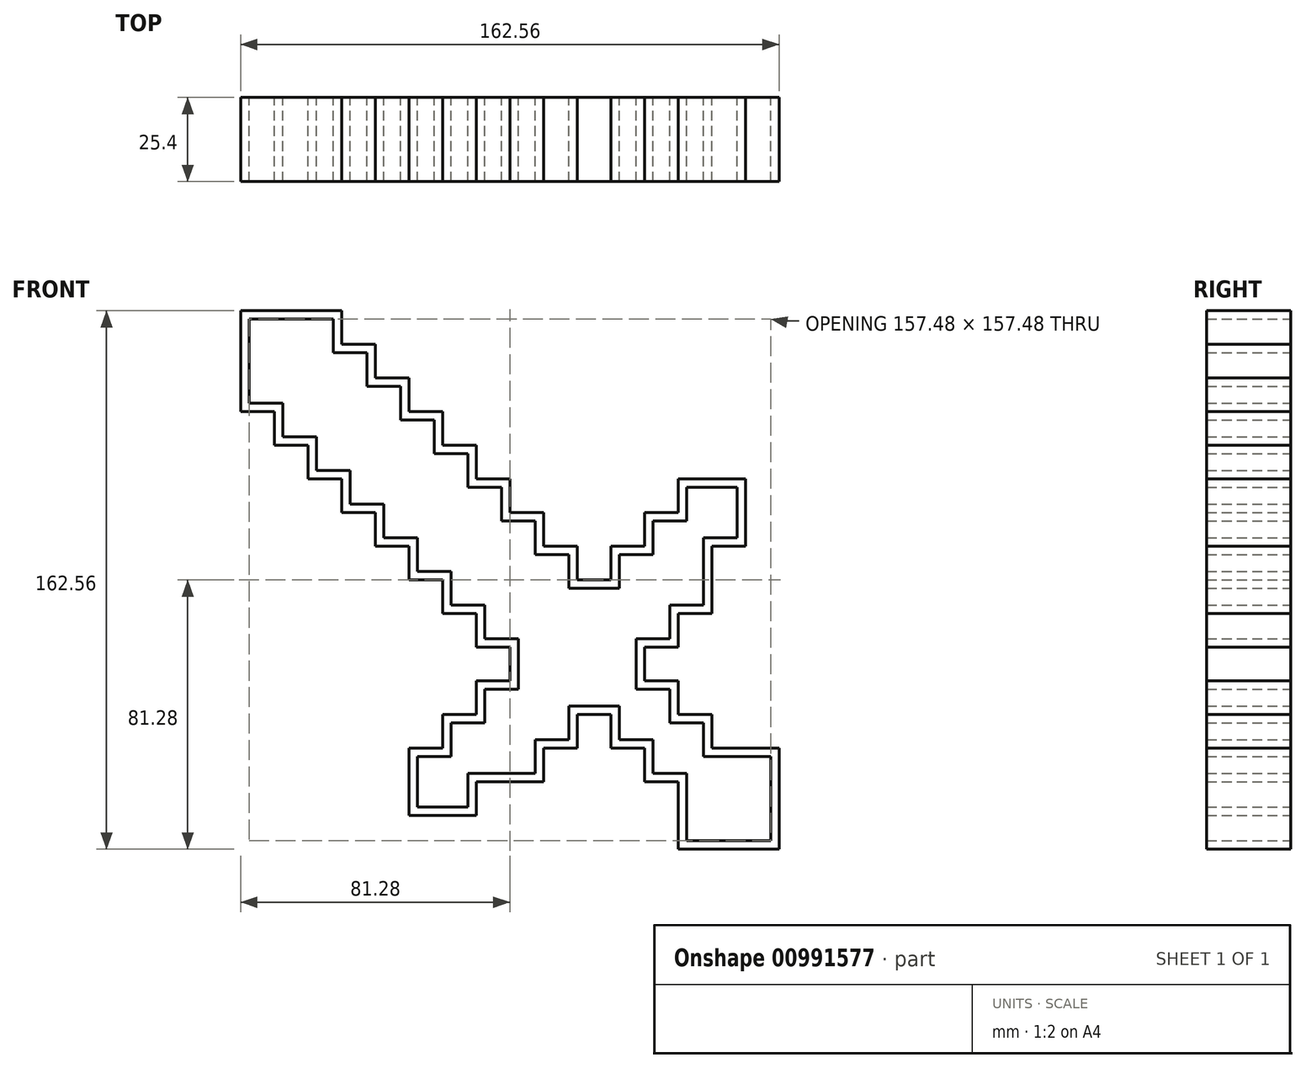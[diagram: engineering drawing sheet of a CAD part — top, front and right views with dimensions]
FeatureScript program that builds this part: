
annotation { "Feature Type Name" : "Feature", "Feature Type Description" : "" }
export const myFeature = defineFeature(function(context is Context, id is Id, definition is map)
    precondition{}
    {
        {
            var Q0;
            Q0=qCreatedBy(makeId("Front.planeOp"),FACE);
            var sketch = newSketch(context, id + "F0", { "sketchPlane" : qUnion([Q0])});
            skLineSegment(sketch, "E0.bottom", {"start": v(-6.87, -60.96) * mm, "end": v(23.61, -60.96) * mm});
            skLineSegment(sketch, "E0.top", {"start": v(3.3, -30.48) * mm, "end": v(23.61, -30.48) * mm});
            skLineSegment(sketch, "E0.left", {"start": v(-6.87, -60.96) * mm, "end": v(-6.87, -40.64) * mm});
            skLineSegment(sketch, "E0.right", {"start": v(23.61, -60.96) * mm, "end": v(23.61, -30.48) * mm});
            skLineSegment(sketch, "E1.bottom", {"start": v(-6.87, -40.64) * mm, "end": v(-17.03, -40.64) * mm});
            skLineSegment(sketch, "E1.top", {"start": v(3.3, -20.32) * mm, "end": v(-17.03, -20.32) * mm});
            skLineSegment(sketch, "E1.left", {"start": v(3.3, -30.48) * mm, "end": v(3.3, -20.32) * mm});
            skLineSegment(sketch, "E1.right", {"start": v(-17.03, -40.64) * mm, "end": v(-17.03, -30.48) * mm});
            skLineSegment(sketch, "E2.bottom", {"start": v(-17.03, -30.48) * mm, "end": v(-27.19, -30.48) * mm});
            skLineSegment(sketch, "E2.top", {"start": v(-6.87, -10.16) * mm, "end": v(-17.03, -10.16) * mm});
            skLineSegment(sketch, "E2.left", {"start": v(-6.87, -20.32) * mm, "end": v(-6.87, -10.16) * mm});
            skLineSegment(sketch, "E2.right", {"start": v(-27.19, -30.48) * mm, "end": v(-27.19, -20.32) * mm});
            skLineSegment(sketch, "E3.bottom", {"start": v(-17.03, -20.32) * mm, "end": v(-57.67, -20.32) * mm});
            skLineSegment(sketch, "E3.top", {"start": v(-27.19, 20.32) * mm, "end": v(-47.5, 20.32) * mm});
            skLineSegment(sketch, "E3.left", {"start": v(-17.03, -10.16) * mm, "end": v(-17.03, 0) * mm});
            skLineSegment(sketch, "E3.right", {"start": v(-57.67, -20.32) * mm, "end": v(-57.67, 0) * mm});
            skLineSegment(sketch, "E4.bottom", {"start": v(-47.5, 20.32) * mm, "end": v(-37.35, 20.32) * mm});
            skLineSegment(sketch, "E5.bottom", {"start": v(-37.35, 0) * mm, "end": v(-67.83, 0) * mm});
            skLineSegment(sketch, "E5.top", {"start": v(-37.35, 30.48) * mm, "end": v(-67.83, 30.48) * mm});
            skLineSegment(sketch, "E5.left", {"start": v(-37.35, 20.32) * mm, "end": v(-37.35, 30.48) * mm});
            skLineSegment(sketch, "E5.right", {"start": v(-67.83, 0) * mm, "end": v(-67.83, 10.16) * mm});
            skPoint(sketch, "E6.oppositeSnap0", {"position": v(-57.67, 10.16) * mm});
            skPoint(sketch, "E6.oppositeSnap1", {"position": v(-47.5, 20.32) * mm});
            skLineSegment(sketch, "E6.bottom", {"start": v(-57.67, 20.32) * mm, "end": v(-47.5, 20.32) * mm});
            skLineSegment(sketch, "E7.bottom", {"start": v(-57.67, 10.16) * mm, "end": v(-77.99, 10.16) * mm});
            skLineSegment(sketch, "E7.top", {"start": v(-47.5, 40.64) * mm, "end": v(-77.99, 40.64) * mm});
            skLineSegment(sketch, "E7.left", {"start": v(-47.5, 30.48) * mm, "end": v(-47.5, 40.64) * mm});
            skLineSegment(sketch, "E7.right", {"start": v(-77.99, 10.16) * mm, "end": v(-77.99, 20.32) * mm});
            skLineSegment(sketch, "E8.bottom", {"start": v(-57.67, 20.32) * mm, "end": v(-88.15, 20.32) * mm});
            skLineSegment(sketch, "E8.top", {"start": v(-57.67, 50.8) * mm, "end": v(-88.15, 50.8) * mm});
            skLineSegment(sketch, "E8.left", {"start": v(-57.67, 40.64) * mm, "end": v(-57.67, 50.8) * mm});
            skLineSegment(sketch, "E8.right", {"start": v(-88.15, 20.32) * mm, "end": v(-88.15, 30.48) * mm});
            skLineSegment(sketch, "E9.bottom", {"start": v(-67.83, 30.48) * mm, "end": v(-98.3, 30.48) * mm});
            skLineSegment(sketch, "E9.top", {"start": v(-67.83, 60.96) * mm, "end": v(-98.3, 60.96) * mm});
            skLineSegment(sketch, "E9.left", {"start": v(-67.83, 50.8) * mm, "end": v(-67.83, 60.96) * mm});
            skLineSegment(sketch, "E9.right", {"start": v(-98.3, 30.48) * mm, "end": v(-98.3, 40.64) * mm});
            skLineSegment(sketch, "E10.bottom", {"start": v(-77.99, 40.64) * mm, "end": v(-108.47, 40.64) * mm});
            skLineSegment(sketch, "E10.top", {"start": v(-77.99, 71.12) * mm, "end": v(-108.47, 71.12) * mm});
            skLineSegment(sketch, "E10.right", {"start": v(-108.47, 40.64) * mm, "end": v(-108.47, 50.8) * mm});
            skLineSegment(sketch, "E11.bottom", {"start": v(-88.15, 50.8) * mm, "end": v(-118.63, 50.8) * mm});
            skLineSegment(sketch, "E11.top", {"start": v(-88.15, 81.28) * mm, "end": v(-98.3, 81.28) * mm});
            skLineSegment(sketch, "E11.left", {"start": v(-88.15, 71.12) * mm, "end": v(-88.15, 81.28) * mm});
            skLineSegment(sketch, "E11.right", {"start": v(-118.63, 50.8) * mm, "end": v(-118.63, 60.96) * mm});
            skLineSegment(sketch, "E12.bottom", {"start": v(-98.3, 60.96) * mm, "end": v(-128.79, 60.96) * mm});
            skLineSegment(sketch, "E12.top", {"start": v(-98.3, 91.44) * mm, "end": v(-108.47, 91.44) * mm});
            skLineSegment(sketch, "E12.left", {"start": v(-98.3, 81.28) * mm, "end": v(-98.3, 91.44) * mm});
            skLineSegment(sketch, "E12.right", {"start": v(-128.79, 60.96) * mm, "end": v(-128.79, 71.12) * mm});
            skLineSegment(sketch, "E13.top", {"start": v(-108.47, 101.6) * mm, "end": v(-138.95, 101.6) * mm});
            skLineSegment(sketch, "E13.left", {"start": v(-108.47, 91.44) * mm, "end": v(-108.47, 101.6) * mm});
            skLineSegment(sketch, "E13.right", {"start": v(-138.95, 71.12) * mm, "end": v(-138.95, 101.6) * mm});
            skLineSegment(sketch, "E14.bottom", {"start": v(-17.03, 20.32) * mm, "end": v(-27.19, 20.32) * mm});
            skLineSegment(sketch, "E15.bottom", {"start": v(-17.03, 0) * mm, "end": v(-6.87, 0) * mm});
            skLineSegment(sketch, "E15.top", {"start": v(-27.19, 30.48) * mm, "end": v(-17.03, 30.48) * mm});
            skLineSegment(sketch, "E15.left", {"start": v(-27.19, 20.32) * mm, "end": v(-27.19, 30.48) * mm});
            skLineSegment(sketch, "E15.right", {"start": v(-6.87, 0) * mm, "end": v(-6.87, 10.16) * mm});
            skLineSegment(sketch, "E16.bottom", {"start": v(-6.87, 10.16) * mm, "end": v(3.3, 10.16) * mm});
            skLineSegment(sketch, "E16.top", {"start": v(-17.03, 40.64) * mm, "end": v(-6.87, 40.64) * mm});
            skLineSegment(sketch, "E16.right", {"start": v(3.3, 10.16) * mm, "end": v(3.3, 30.48) * mm});
            skLineSegment(sketch, "E17.bottom", {"start": v(3.3, 30.48) * mm, "end": v(13.45, 30.48) * mm});
            skLineSegment(sketch, "E17.top", {"start": v(-6.87, 50.8) * mm, "end": v(13.45, 50.8) * mm});
            skLineSegment(sketch, "E17.left", {"start": v(-6.87, 40.64) * mm, "end": v(-6.87, 50.8) * mm});
            skLineSegment(sketch, "E17.right", {"start": v(13.45, 30.48) * mm, "end": v(13.45, 50.8) * mm});
            skLineSegment(sketch, "E18", {"start": v(-138.95, 101.6) * mm, "end": v(-128.79, 91.44) * mm});
            skLineSegment(sketch, "E19.trimOffspring", {"start": v(-17.03, 30.48) * mm, "end": v(-17.03, 40.64) * mm});
            skPoint(sketch, "E20.orphan", {"position": v(-6.87, 30.48) * mm});
            skPoint(sketch, "E16.left.start.orphan", {"position": v(-17.03, 10.16) * mm});
            skPoint(sketch, "E21.orphan", {"position": v(-47.5, 10.16) * mm});
            skLineSegment(sketch, "E22.trimOffspring", {"start": v(-77.99, 60.96) * mm, "end": v(-77.99, 71.12) * mm});
            skLineSegment(sketch, "E23.trimOffspring", {"start": v(-128.79, 71.12) * mm, "end": v(-138.95, 71.12) * mm});
            skLineSegment(sketch, "E24.MirrorCS", {"start": v(-57.67, -10.16) * mm, "end": v(-67.83, -10.16) * mm});
            skLineSegment(sketch, "E25.MirrorCS", {"start": v(-67.83, -10.16) * mm, "end": v(-67.83, -20.32) * mm});
            skLineSegment(sketch, "E26.MirrorCS", {"start": v(-67.83, -20.32) * mm, "end": v(-77.99, -20.32) * mm});
            skLineSegment(sketch, "E27.MirrorCS", {"start": v(-77.99, -20.32) * mm, "end": v(-77.99, -30.48) * mm});
            skLineSegment(sketch, "E28.MirrorCS", {"start": v(-88.15, -30.48) * mm, "end": v(-88.15, -50.8) * mm});
            skLineSegment(sketch, "E29.MirrorCS", {"start": v(-67.83, -50.8) * mm, "end": v(-88.15, -50.8) * mm});
            skLineSegment(sketch, "E30.MirrorCS", {"start": v(-67.83, -40.64) * mm, "end": v(-67.83, -50.8) * mm});
            skLineSegment(sketch, "E31.MirrorCS", {"start": v(-47.5, -40.64) * mm, "end": v(-67.83, -40.64) * mm});
            skLineSegment(sketch, "E32.MirrorCS", {"start": v(-47.5, -30.48) * mm, "end": v(-47.5, -40.64) * mm});
            skLineSegment(sketch, "E33.MirrorCS", {"start": v(-37.35, -20.32) * mm, "end": v(-37.35, -30.48) * mm});
            skLineSegment(sketch, "E34.MirrorCS", {"start": v(-77.99, -30.48) * mm, "end": v(-88.15, -30.48) * mm});
            skLineSegment(sketch, "E35.MirrorCS", {"start": v(-37.35, -30.48) * mm, "end": v(-47.5, -30.48) * mm});
            skSolve(sketch);
        }
        {
            var Q0;
            Q0 = qSketchRegion(id + "F0", true);
            extrude(context, id + "F1", {"entities" : qUnion([Q0]), "depth" : 25.4 * mm, "offsetDistance" : 25.4 * mm});
        }
        {
            var Q0;
            Q0=makeQuery(id+"F1.opExtrude","CAP_FACE",FACE,{"disambiguationData":[OSD([sQuery(id+"F0.wireOp",EDGE,"E0.bottom"),sQuery(id+"F0.wireOp",EDGE,"E0.top"),sQuery(id+"F0.wireOp",EDGE,"E0.left"),sQuery(id+"F0.wireOp",EDGE,"E0.right"),sQuery(id+"F0.wireOp",EDGE,"E1.bottom"),sQuery(id+"F0.wireOp",EDGE,"E1.top"),sQuery(id+"F0.wireOp",EDGE,"E1.left"),sQuery(id+"F0.wireOp",EDGE,"E1.right"),sQuery(id+"F0.wireOp",EDGE,"E2.bottom"),sQuery(id+"F0.wireOp",EDGE,"E2.top"),sQuery(id+"F0.wireOp",EDGE,"E2.left"),sQuery(id+"F0.wireOp",EDGE,"E2.right"),sQuery(id+"F0.wireOp",EDGE,"E3.bottom"),sQuery(id+"F0.wireOp",EDGE,"E3.top"),sQuery(id+"F0.wireOp",EDGE,"E3.left"),sQuery(id+"F0.wireOp",EDGE,"E3.right"),sQuery(id+"F0.wireOp",EDGE,"E5.bottom"),sQuery(id+"F0.wireOp",EDGE,"E5.top"),sQuery(id+"F0.wireOp",EDGE,"E5.left"),sQuery(id+"F0.wireOp",EDGE,"E5.right"),sQuery(id+"F0.wireOp",EDGE,"E7.bottom"),sQuery(id+"F0.wireOp",EDGE,"E7.top"),sQuery(id+"F0.wireOp",EDGE,"E7.left"),sQuery(id+"F0.wireOp",EDGE,"E7.right"),sQuery(id+"F0.wireOp",EDGE,"E8.bottom"),sQuery(id+"F0.wireOp",EDGE,"E8.top"),sQuery(id+"F0.wireOp",EDGE,"E8.left"),sQuery(id+"F0.wireOp",EDGE,"E8.right"),sQuery(id+"F0.wireOp",EDGE,"E9.bottom"),sQuery(id+"F0.wireOp",EDGE,"E9.top"),sQuery(id+"F0.wireOp",EDGE,"E9.left"),sQuery(id+"F0.wireOp",EDGE,"E9.right"),sQuery(id+"F0.wireOp",EDGE,"E10.bottom"),sQuery(id+"F0.wireOp",EDGE,"E10.top"),sQuery(id+"F0.wireOp",EDGE,"E10.right"),sQuery(id+"F0.wireOp",EDGE,"E11.bottom"),sQuery(id+"F0.wireOp",EDGE,"E11.top"),sQuery(id+"F0.wireOp",EDGE,"E11.left"),sQuery(id+"F0.wireOp",EDGE,"E11.right"),sQuery(id+"F0.wireOp",EDGE,"E12.bottom"),sQuery(id+"F0.wireOp",EDGE,"E12.top"),sQuery(id+"F0.wireOp",EDGE,"E12.left"),sQuery(id+"F0.wireOp",EDGE,"E12.right"),sQuery(id+"F0.wireOp",EDGE,"E13.top"),sQuery(id+"F0.wireOp",EDGE,"E13.left"),sQuery(id+"F0.wireOp",EDGE,"E13.right"),sQuery(id+"F0.wireOp",EDGE,"E15.bottom"),sQuery(id+"F0.wireOp",EDGE,"E15.top"),sQuery(id+"F0.wireOp",EDGE,"E15.left"),sQuery(id+"F0.wireOp",EDGE,"E15.right"),sQuery(id+"F0.wireOp",EDGE,"E16.bottom"),sQuery(id+"F0.wireOp",EDGE,"E16.top"),sQuery(id+"F0.wireOp",EDGE,"E16.right"),sQuery(id+"F0.wireOp",EDGE,"E17.bottom"),sQuery(id+"F0.wireOp",EDGE,"E17.top"),sQuery(id+"F0.wireOp",EDGE,"E17.left"),sQuery(id+"F0.wireOp",EDGE,"E17.right"),sQuery(id+"F0.wireOp",EDGE,"E19.trimOffspring"),sQuery(id+"F0.wireOp",EDGE,"E22.trimOffspring"),sQuery(id+"F0.wireOp",EDGE,"E23.trimOffspring"),sQuery(id+"F0.wireOp",EDGE,"E24.MirrorCS"),sQuery(id+"F0.wireOp",EDGE,"E25.MirrorCS"),sQuery(id+"F0.wireOp",EDGE,"E28.MirrorCS"),sQuery(id+"F0.wireOp",EDGE,"E29.MirrorCS"),sQuery(id+"F0.wireOp",EDGE,"E30.MirrorCS"),sQuery(id+"F0.wireOp",EDGE,"E31.MirrorCS"),sQuery(id+"F0.wireOp",EDGE,"E32.MirrorCS"),sQuery(id+"F0.wireOp",EDGE,"E33.MirrorCS"),sQuery(id+"F0.wireOp",EDGE,"E26.MirrorCS"),sQuery(id+"F0.wireOp",EDGE,"E27.MirrorCS"),sQuery(id+"F0.wireOp",EDGE,"E34.MirrorCS"),sQuery(id+"F0.wireOp",EDGE,"E35.MirrorCS")])],"isStart":false});
            var Q1;
            Q1=makeQuery(id+"F1.opExtrude","CAP_FACE",FACE,{"disambiguationData":[OSD([sQuery(id+"F0.wireOp",EDGE,"E0.bottom"),sQuery(id+"F0.wireOp",EDGE,"E0.top"),sQuery(id+"F0.wireOp",EDGE,"E0.left"),sQuery(id+"F0.wireOp",EDGE,"E0.right"),sQuery(id+"F0.wireOp",EDGE,"E1.bottom"),sQuery(id+"F0.wireOp",EDGE,"E1.top"),sQuery(id+"F0.wireOp",EDGE,"E1.left"),sQuery(id+"F0.wireOp",EDGE,"E1.right"),sQuery(id+"F0.wireOp",EDGE,"E2.bottom"),sQuery(id+"F0.wireOp",EDGE,"E2.top"),sQuery(id+"F0.wireOp",EDGE,"E2.left"),sQuery(id+"F0.wireOp",EDGE,"E2.right"),sQuery(id+"F0.wireOp",EDGE,"E3.bottom"),sQuery(id+"F0.wireOp",EDGE,"E3.top"),sQuery(id+"F0.wireOp",EDGE,"E3.left"),sQuery(id+"F0.wireOp",EDGE,"E3.right"),sQuery(id+"F0.wireOp",EDGE,"E5.bottom"),sQuery(id+"F0.wireOp",EDGE,"E5.top"),sQuery(id+"F0.wireOp",EDGE,"E5.left"),sQuery(id+"F0.wireOp",EDGE,"E5.right"),sQuery(id+"F0.wireOp",EDGE,"E7.bottom"),sQuery(id+"F0.wireOp",EDGE,"E7.top"),sQuery(id+"F0.wireOp",EDGE,"E7.left"),sQuery(id+"F0.wireOp",EDGE,"E7.right"),sQuery(id+"F0.wireOp",EDGE,"E8.bottom"),sQuery(id+"F0.wireOp",EDGE,"E8.top"),sQuery(id+"F0.wireOp",EDGE,"E8.left"),sQuery(id+"F0.wireOp",EDGE,"E8.right"),sQuery(id+"F0.wireOp",EDGE,"E9.bottom"),sQuery(id+"F0.wireOp",EDGE,"E9.top"),sQuery(id+"F0.wireOp",EDGE,"E9.left"),sQuery(id+"F0.wireOp",EDGE,"E9.right"),sQuery(id+"F0.wireOp",EDGE,"E10.bottom"),sQuery(id+"F0.wireOp",EDGE,"E10.top"),sQuery(id+"F0.wireOp",EDGE,"E10.right"),sQuery(id+"F0.wireOp",EDGE,"E11.bottom"),sQuery(id+"F0.wireOp",EDGE,"E11.top"),sQuery(id+"F0.wireOp",EDGE,"E11.left"),sQuery(id+"F0.wireOp",EDGE,"E11.right"),sQuery(id+"F0.wireOp",EDGE,"E12.bottom"),sQuery(id+"F0.wireOp",EDGE,"E12.top"),sQuery(id+"F0.wireOp",EDGE,"E12.left"),sQuery(id+"F0.wireOp",EDGE,"E12.right"),sQuery(id+"F0.wireOp",EDGE,"E13.top"),sQuery(id+"F0.wireOp",EDGE,"E13.left"),sQuery(id+"F0.wireOp",EDGE,"E13.right"),sQuery(id+"F0.wireOp",EDGE,"E15.bottom"),sQuery(id+"F0.wireOp",EDGE,"E15.top"),sQuery(id+"F0.wireOp",EDGE,"E15.left"),sQuery(id+"F0.wireOp",EDGE,"E15.right"),sQuery(id+"F0.wireOp",EDGE,"E16.bottom"),sQuery(id+"F0.wireOp",EDGE,"E16.top"),sQuery(id+"F0.wireOp",EDGE,"E16.right"),sQuery(id+"F0.wireOp",EDGE,"E17.bottom"),sQuery(id+"F0.wireOp",EDGE,"E17.top"),sQuery(id+"F0.wireOp",EDGE,"E17.left"),sQuery(id+"F0.wireOp",EDGE,"E17.right"),sQuery(id+"F0.wireOp",EDGE,"E19.trimOffspring"),sQuery(id+"F0.wireOp",EDGE,"E22.trimOffspring"),sQuery(id+"F0.wireOp",EDGE,"E23.trimOffspring"),sQuery(id+"F0.wireOp",EDGE,"E24.MirrorCS"),sQuery(id+"F0.wireOp",EDGE,"E25.MirrorCS"),sQuery(id+"F0.wireOp",EDGE,"E28.MirrorCS"),sQuery(id+"F0.wireOp",EDGE,"E29.MirrorCS"),sQuery(id+"F0.wireOp",EDGE,"E30.MirrorCS"),sQuery(id+"F0.wireOp",EDGE,"E31.MirrorCS"),sQuery(id+"F0.wireOp",EDGE,"E32.MirrorCS"),sQuery(id+"F0.wireOp",EDGE,"E33.MirrorCS"),sQuery(id+"F0.wireOp",EDGE,"E26.MirrorCS"),sQuery(id+"F0.wireOp",EDGE,"E27.MirrorCS"),sQuery(id+"F0.wireOp",EDGE,"E34.MirrorCS"),sQuery(id+"F0.wireOp",EDGE,"E35.MirrorCS")])],"isStart":true});
            shell(context, id + "F2", {"entities" : qUnion([Q0, Q1]), "thickness" : 2.54 * mm});
        }
    });
